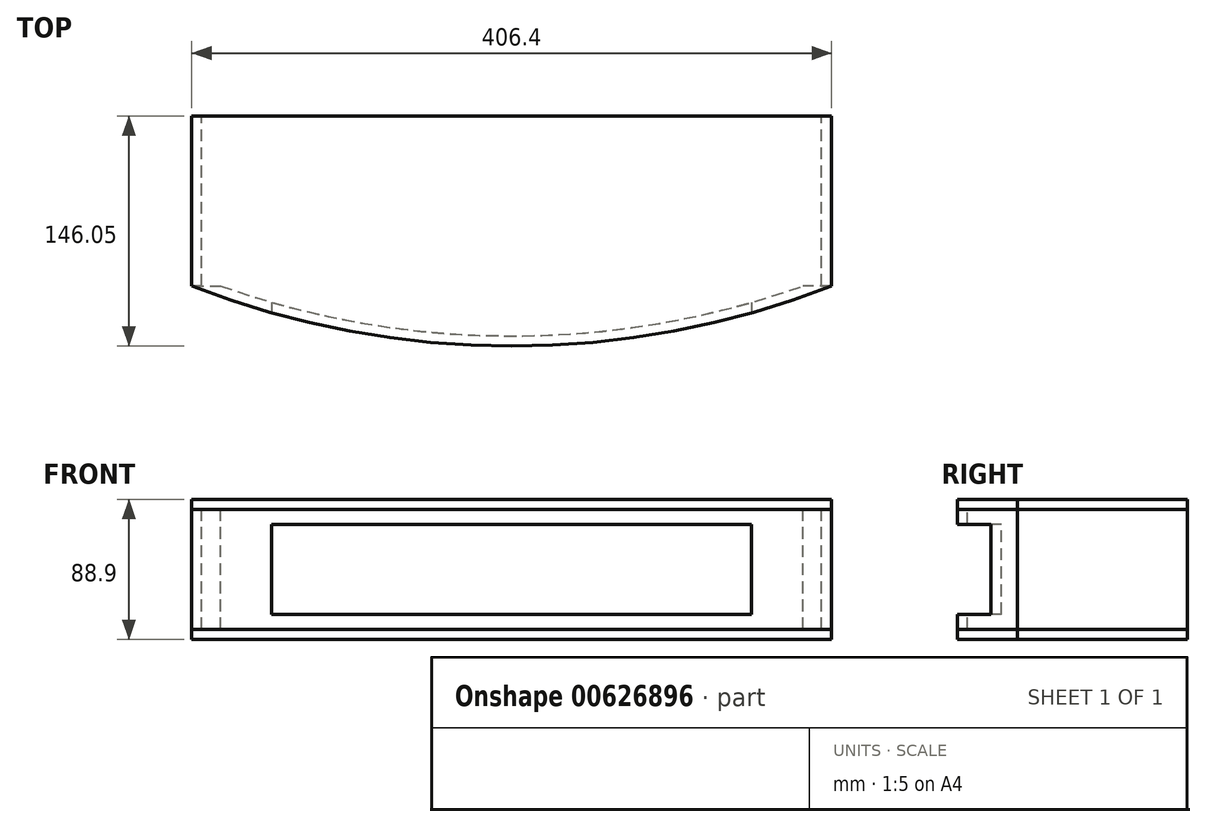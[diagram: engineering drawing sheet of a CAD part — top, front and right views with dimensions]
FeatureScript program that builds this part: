
annotation { "Feature Type Name" : "Feature", "Feature Type Description" : "" }
export const myFeature = defineFeature(function(context is Context, id is Id, definition is map)
    precondition{}
    {
        {
            var Q0;
            Q0=qCreatedBy(makeId("Top.planeOp"),FACE);
            var sketch = newSketch(context, id + "F0", { "sketchPlane" : qUnion([Q0])});
            skLineSegment(sketch, "E0.bottom", {"start": v(203.2, -53.97) * mm, "end": v(-203.2, -53.98) * mm, "construction": true});
            skLineSegment(sketch, "E0.top", {"start": v(203.2, 53.98) * mm, "end": v(-203.2, 53.97) * mm});
            skLineSegment(sketch, "E0.left", {"start": v(203.2, -53.97) * mm, "end": v(203.2, 53.98) * mm});
            skLineSegment(sketch, "E0.right", {"start": v(-203.2, -53.98) * mm, "end": v(-203.2, 53.97) * mm});
            skPoint(sketch, "E0.middle", {"position": v(0, 0) * mm});
            skLineSegment(sketch, "E1", {"start": v(0, -53.98) * mm, "end": v(0, -92.08) * mm, "construction": true});
            skArc(sketch, "E2", {"start": v(-203.2, -53.97) * mm, "mid": v(0, -92.07) * mm, "end": v(203.2, -53.97) * mm});
            skSolve(sketch);
        }
        {
            var Q0;
            Q0=makeQuery(id+"F0.imprint","IMPRINT",FACE,{"disambiguationData":[TD([[makeQuery(id+"F0.imprint","IMPRINT",EDGE,{"derivedFrom":sQuery(id+"F0.wireOp",EDGE,"E0.top")}),1.0]])]});
            extrude(context, id + "F1", {"entities" : qUnion([Q0]), "depth" : 6.35 * mm, "offsetDistance" : 25.4 * mm});
        }
        {
            var Q0;
            Q0=makeQuery(id+"F1.opExtrude","CAP_FACE",FACE,{"disambiguationData":[OSD([sQuery(id+"F0.wireOp",EDGE,"E0.top"),sQuery(id+"F0.wireOp",EDGE,"E0.left"),sQuery(id+"F0.wireOp",EDGE,"E0.right"),sQuery(id+"F0.wireOp",EDGE,"E2")])],"isStart":true});
            var sketch = newSketch(context, id + "F2", { "sketchPlane" : qUnion([Q0])});
            skLineSegment(sketch, "E3", {"start": v(-203.2, 53.98) * mm, "end": v(-184.95, 53.98) * mm, "construction": true});
            skLineSegment(sketch, "E4", {"start": v(0, 53.98) * mm, "end": v(0, 92.07) * mm, "construction": true});
            skArc(sketch, "E5", {"start": v(203.2, 53.97) * mm, "mid": v(0, 92.07) * mm, "end": v(-203.2, 53.98) * mm, "construction": true});
            skArc(sketch, "E6.0", {"start": v(184.95, 53.98) * mm, "mid": v(0, 85.73) * mm, "end": v(-184.95, 53.98) * mm});
            skLineSegment(sketch, "E7", {"start": v(203.2, 53.97) * mm, "end": v(184.95, 53.97) * mm});
            skLineSegment(sketch, "E8", {"start": v(-203.2, 53.98) * mm, "end": v(-184.95, 53.98) * mm});
            skLineSegment(sketch, "E9.trimOffspring", {"start": v(-153.01, 53.98) * mm, "end": v(166.13, 53.97) * mm, "construction": true});
            skLineSegment(sketch, "E10.trimOffspring", {"start": v(184.95, 53.97) * mm, "end": v(203.2, 53.97) * mm, "construction": true});
            skSolve(sketch);
        }
        {
            var Q0;
            Q0 = qSketchRegion(id + "F2", true);
            var Q1;
            Q1=makeQuery(id+"F2.imprint","IMPRINT",FACE,{"disambiguationData":[TD([[makeQuery(id+"F2.imprint","IMPRINT",EDGE,{"derivedFrom":sQuery(id+"F2.wireOp",EDGE,"E6.0")}),-1.0]])]});
            extrude(context, id + "F3", {"entities" : qUnion([Q0, Q1]), "depth" : 76.2 * mm, "offsetDistance" : 25.4 * mm});
        }
        {
            var Q0;
            Q0=makeQuery(id+"F1.opExtrude","CAP_FACE",FACE,{"disambiguationData":[OSD([sQuery(id+"F0.wireOp",EDGE,"E0.top"),sQuery(id+"F0.wireOp",EDGE,"E0.left"),sQuery(id+"F0.wireOp",EDGE,"E0.right"),sQuery(id+"F0.wireOp",EDGE,"E2")])],"isStart":true});
            cPlane(context, id + "F4", {"entities" : qUnion([Q0]), "cplaneType" : CPlaneType.OFFSET, "offset" : 38.1 * mm, "width" : 152.4 * mm, "height" : 152.4 * mm});
        }
        {
            var Q0;
            Q0=makeQuery(id+"F1.opExtrude","SWEPT_BODY",BODY,{"disambiguationData":[OSD([sQuery(id+"F0.wireOp",EDGE,"E0.top"),sQuery(id+"F0.wireOp",EDGE,"E0.left"),sQuery(id+"F0.wireOp",EDGE,"E0.right"),sQuery(id+"F0.wireOp",EDGE,"E2")])]});
            var Q1;
            Q1=qCreatedBy(id+"F4.planeOp",FACE);
            mirror(context, id + "F5", {"entities" : qUnion([Q0]), "mirrorPlane" : qUnion([Q1])});
        }
        {
            var Q0;
            Q0=makeQuery(id+"F5.opPattern","COPY",FACE,{"derivedFrom":makeQuery(id+"F1.opExtrude","SWEPT_FACE",FACE,{"disambiguationData":[OSD([sQuery(id+"F0.wireOp",EDGE,"E0.right")])]}),"instanceName":"1"});
            var sketch = newSketch(context, id + "F6", { "sketchPlane" : qUnion([Q0])});
            skLineSegment(sketch, "E11", {"start": v(53.98, -76.2) * mm, "end": v(53.98, 0) * mm});
            skLineSegment(sketch, "E12", {"start": v(53.98, 0) * mm, "end": v(-53.97, 0) * mm});
            skLineSegment(sketch, "E13", {"start": v(-53.97, 0) * mm, "end": v(-53.97, -76.2) * mm});
            skLineSegment(sketch, "E14", {"start": v(-53.97, -76.2) * mm, "end": v(53.98, -76.2) * mm});
            skSolve(sketch);
        }
        {
            var Q0;
            Q0 = qSketchRegion(id + "F6", true);
            extrude(context, id + "F7", {"entities" : qUnion([Q0]), "oppositeDirection" : true, "depth" : 6.35 * mm, "offsetDistance" : 25.4 * mm});
        }
        {
            var Q0;
            Q0=makeQuery(id+"F7.opExtrude","SWEPT_BODY",BODY,{"disambiguationData":[OSD([sQuery(id+"F6.wireOp",EDGE,"E11"),sQuery(id+"F6.wireOp",EDGE,"E12"),sQuery(id+"F6.wireOp",EDGE,"E13"),sQuery(id+"F6.wireOp",EDGE,"E14")])]});
            var Q1;
            Q1=qCreatedBy(makeId("Right.planeOp"),FACE);
            mirror(context, id + "F8", {"entities" : qUnion([Q0]), "mirrorPlane" : qUnion([Q1])});
        }
        {
            var Q0;
            Q0=makeQuery(id+"F8.opPattern","COPY",FACE,{"derivedFrom":makeQuery(id+"F7.opExtrude","SWEPT_FACE",FACE,{"disambiguationData":[OSD([sQuery(id+"F6.wireOp",EDGE,"E11")])]}),"instanceName":"1"});
            cPlane(context, id + "F9", {"entities" : qUnion([Q0]), "cplaneType" : CPlaneType.OFFSET, "offset" : 38.1 * mm, "width" : 152.4 * mm, "height" : 152.4 * mm});
        }
        {
            var Q0;
            Q0=qCreatedBy(id+"F9.planeOp",FACE);
            var sketch = newSketch(context, id + "F10", { "sketchPlane" : qUnion([Q0])});
            skLineSegment(sketch, "E15", {"start": v(0, 0) * mm, "end": v(0, -38.1) * mm, "construction": true});
            skLineSegment(sketch, "E16.bottom", {"start": v(152.4, -66.68) * mm, "end": v(-152.4, -66.68) * mm});
            skLineSegment(sketch, "E16.top", {"start": v(152.4, -9.52) * mm, "end": v(-152.4, -9.52) * mm});
            skLineSegment(sketch, "E16.left", {"start": v(152.4, -66.68) * mm, "end": v(152.4, -9.52) * mm});
            skLineSegment(sketch, "E16.right", {"start": v(-152.4, -66.68) * mm, "end": v(-152.4, -9.52) * mm});
            skPoint(sketch, "E16.middle", {"position": v(0, -38.1) * mm});
            skSolve(sketch);
        }
        {
            var Q0;
            Q0 = qSketchRegion(id + "F10", true);
            extrude(context, id + "F11", {"entities" : qUnion([Q0]), "operationType" : NewBodyOperationType.REMOVE, "endBound" : BoundingType.THROUGH_ALL, "oppositeDirection" : true, "depth" : 25.4 * mm, "offsetDistance" : 25.4 * mm});
        }
    });
